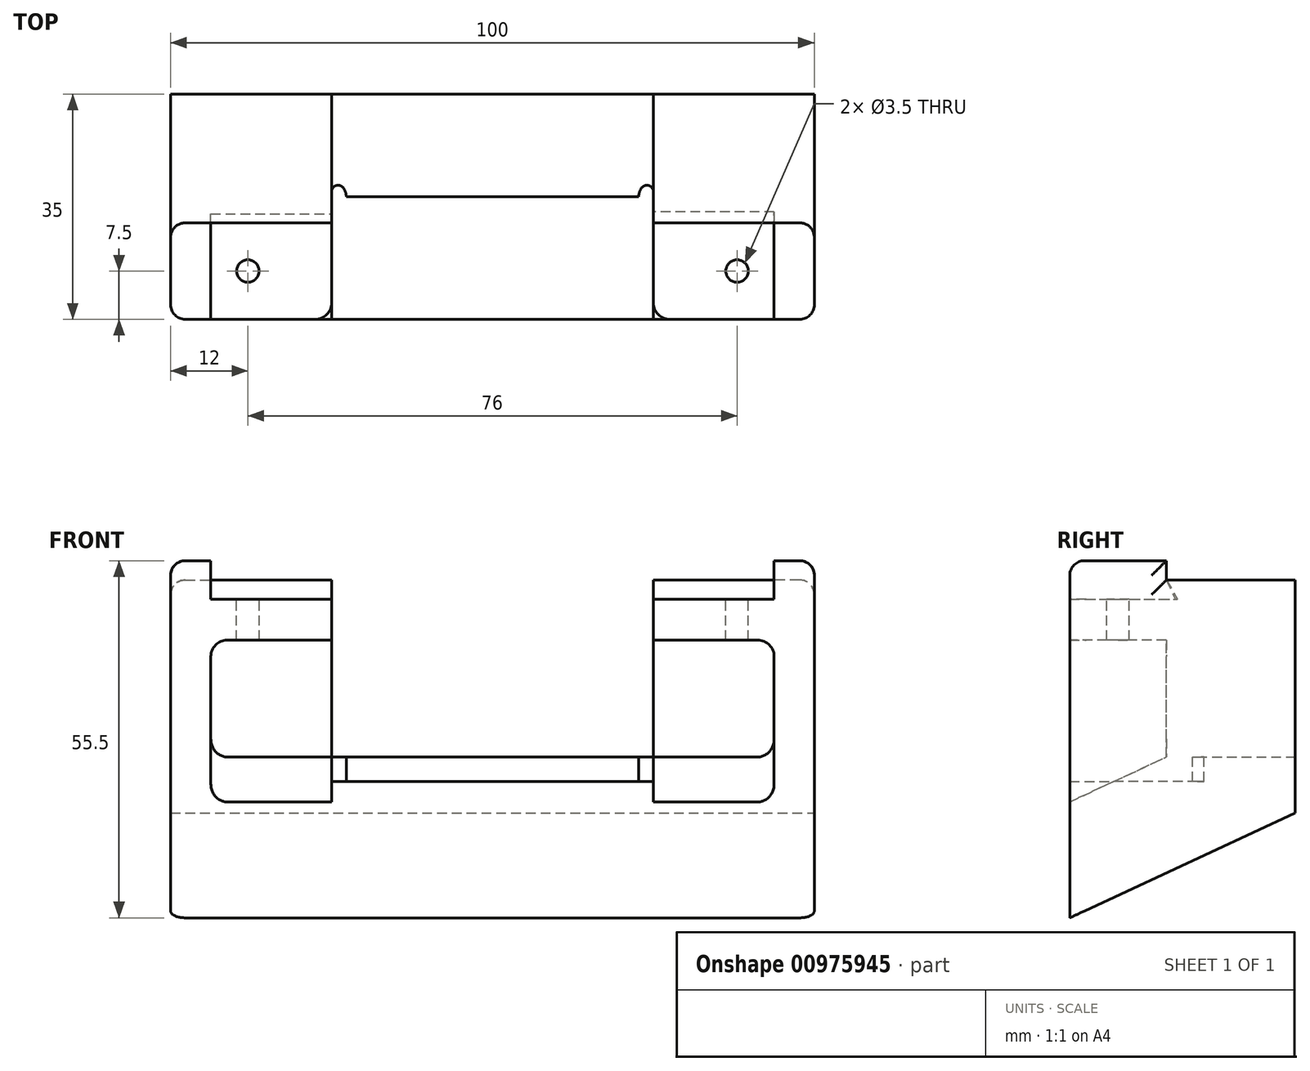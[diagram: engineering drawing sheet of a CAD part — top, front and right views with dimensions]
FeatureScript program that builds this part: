
annotation { "Feature Type Name" : "Feature", "Feature Type Description" : "" }
export const myFeature = defineFeature(function(context is Context, id is Id, definition is map)
    precondition{}
    {
        {
            var Q0;
            Q0=qCreatedBy(makeId("Front.planeOp"),FACE);
            var sketch = newSketch(context, id + "F0", { "sketchPlane" : qUnion([Q0])});
            skLineSegment(sketch, "E0", {"start": v(0, 0) * mm, "end": v(0, 100) * mm, "construction": true});
            skLineSegment(sketch, "E1", {"start": v(0, 25) * mm, "end": v(-25, 25) * mm});
            skLineSegment(sketch, "E2", {"start": v(-25, 25) * mm, "end": v(-25, 49.5) * mm});
            skLineSegment(sketch, "E3", {"start": v(-25, 49.5) * mm, "end": v(-43.75, 49.5) * mm});
            skLineSegment(sketch, "E4", {"start": v(-43.75, 49.5) * mm, "end": v(-43.75, 55.5) * mm});
            skLineSegment(sketch, "E5", {"start": v(-43.75, 55.5) * mm, "end": v(-50, 55.5) * mm});
            skLineSegment(sketch, "E6", {"start": v(-50, 55.5) * mm, "end": v(-50, 0) * mm});
            skLineSegment(sketch, "E7", {"start": v(-50, 0) * mm, "end": v(0, 0) * mm});
            skLineSegment(sketch, "E8.MirrorCS", {"start": v(25, 25) * mm, "end": v(25, 49.5) * mm});
            skLineSegment(sketch, "E9.MirrorCS", {"start": v(50, 55.5) * mm, "end": v(50, 0) * mm});
            skLineSegment(sketch, "E10.MirrorCS", {"start": v(0, 25) * mm, "end": v(25, 25) * mm});
            skLineSegment(sketch, "E11.MirrorCS", {"start": v(43.75, 55.5) * mm, "end": v(50, 55.5) * mm});
            skLineSegment(sketch, "E12.MirrorCS", {"start": v(25, 49.5) * mm, "end": v(43.75, 49.5) * mm});
            skLineSegment(sketch, "E13.MirrorCS", {"start": v(43.75, 49.5) * mm, "end": v(43.75, 55.5) * mm});
            skLineSegment(sketch, "E14.MirrorCS", {"start": v(50, 0) * mm, "end": v(0, 0) * mm});
            skSolve(sketch);
        }
        {
            var Q0;
            Q0 = qSketchRegion(id + "F0", true);
            extrude(context, id + "F1", {"entities" : qUnion([Q0]), "depth" : 15 * mm, "offsetDistance" : 25.4 * mm});
        }
        {
            var Q0;
            Q0=makeQuery(id+"F1.opExtrude","CAP_FACE",FACE,{"disambiguationData":[OSD([sQuery(id+"F0.wireOp",EDGE,"E1"),sQuery(id+"F0.wireOp",EDGE,"E2"),sQuery(id+"F0.wireOp",EDGE,"E3"),sQuery(id+"F0.wireOp",EDGE,"E4"),sQuery(id+"F0.wireOp",EDGE,"E5"),sQuery(id+"F0.wireOp",EDGE,"E6"),sQuery(id+"F0.wireOp",EDGE,"E7"),sQuery(id+"F0.wireOp",EDGE,"E8.MirrorCS"),sQuery(id+"F0.wireOp",EDGE,"E9.MirrorCS"),sQuery(id+"F0.wireOp",EDGE,"E10.MirrorCS"),sQuery(id+"F0.wireOp",EDGE,"E11.MirrorCS"),sQuery(id+"F0.wireOp",EDGE,"E12.MirrorCS"),sQuery(id+"F0.wireOp",EDGE,"E13.MirrorCS"),sQuery(id+"F0.wireOp",EDGE,"E14.MirrorCS")])],"isStart":true});
            var sketch = newSketch(context, id + "F2", { "sketchPlane" : qUnion([Q0])});
            skLineSegment(sketch, "E15.0", {"start": v(-50, 52.5) * mm, "end": v(-50, 0) * mm});
            skLineSegment(sketch, "E15.1", {"start": v(0, 0) * mm, "end": v(-50, 0) * mm});
            skLineSegment(sketch, "E16", {"start": v(-50, 52.5) * mm, "end": v(-25, 52.5) * mm});
            skLineSegment(sketch, "E17", {"start": v(-25, 52.5) * mm, "end": v(-25, 25) * mm});
            skLineSegment(sketch, "E18", {"start": v(-25, 25) * mm, "end": v(0, 25) * mm});
            skLineSegment(sketch, "E19", {"start": v(0, 0) * mm, "end": v(0, 25) * mm, "construction": true});
            skLineSegment(sketch, "E20.MirrorCS", {"start": v(25, 25) * mm, "end": v(0, 25) * mm});
            skLineSegment(sketch, "E21.MirrorCS", {"start": v(25, 52.5) * mm, "end": v(25, 25) * mm});
            skLineSegment(sketch, "E22.MirrorCS", {"start": v(50, 52.5) * mm, "end": v(25, 52.5) * mm});
            skLineSegment(sketch, "E23.MirrorCS", {"start": v(50, 52.5) * mm, "end": v(50, 0) * mm});
            skLineSegment(sketch, "E24.MirrorCS", {"start": v(0, 0) * mm, "end": v(50, 0) * mm});
            skPoint(sketch, "E25.orphan", {"position": v(-50, 55.5) * mm});
            skPoint(sketch, "E26.orphan", {"position": v(50, 55.5) * mm});
            skSolve(sketch);
        }
        {
            var Q0;
            Q0 = qSketchRegion(id + "F2", true);
            extrude(context, id + "F3", {"entities" : qUnion([Q0]), "operationType" : NewBodyOperationType.ADD, "depth" : 20 * mm, "offsetDistance" : 25.4 * mm});
        }
        {
            var Q0;
            Q0=makeQuery(id+"F3.boolean.opBoolean","MERGE",FACE,{"derivedFrom":[makeQuery(id+"F1.opExtrude","SWEPT_FACE",FACE,{"disambiguationData":[OSD([sQuery(id+"F0.wireOp",EDGE,"E9.MirrorCS")])]}),makeQuery(id+"F3.opExtrude","SWEPT_FACE",FACE,{"disambiguationData":[OSD([sQuery(id+"F2.wireOp",EDGE,"E15.0")])]})]});
            var sketch = newSketch(context, id + "F4", { "sketchPlane" : qUnion([Q0])});
            skLineSegment(sketch, "E27", {"start": v(20, 0) * mm, "end": v(-15, 0) * mm});
            skLineSegment(sketch, "E28", {"start": v(-15, 0) * mm, "end": v(20, 16.32) * mm});
            skLineSegment(sketch, "E29", {"start": v(20, 16.32) * mm, "end": v(20, 0) * mm});
            skSolve(sketch);
        }
        {
            var Q0;
            Q0 = qSketchRegion(id + "F4", true);
            extrude(context, id + "F5", {"entities" : qUnion([Q0]), "operationType" : NewBodyOperationType.REMOVE, "endBound" : BoundingType.UP_TO_NEXT, "oppositeDirection" : true, "depth" : 25.4 * mm, "offsetDistance" : 25.4 * mm});
        }
        {
            var Q0;
            Q0=makeQuery(id+"F3.boolean.opBoolean","MERGE",FACE,{"derivedFrom":[makeQuery(id+"F1.opExtrude","SWEPT_FACE",FACE,{"disambiguationData":[OSD([sQuery(id+"F0.wireOp",EDGE,"E6")])]}),makeQuery(id+"F3.opExtrude","SWEPT_FACE",FACE,{"disambiguationData":[OSD([sQuery(id+"F2.wireOp",EDGE,"E23.MirrorCS")])]})]});
            cPlane(context, id + "F6", {"entities" : qUnion([Q0]), "cplaneType" : CPlaneType.OFFSET, "offset" : 56 * mm, "oppositeDirection" : true, "width" : 152.4 * mm, "height" : 152.4 * mm});
        }
        {
            var Q0;
            Q0=makeQuery(id+"F1.opExtrude","CAP_FACE",FACE,{"disambiguationData":[OSD([sQuery(id+"F0.wireOp",EDGE,"E1"),sQuery(id+"F0.wireOp",EDGE,"E2"),sQuery(id+"F0.wireOp",EDGE,"E3"),sQuery(id+"F0.wireOp",EDGE,"E4"),sQuery(id+"F0.wireOp",EDGE,"E5"),sQuery(id+"F0.wireOp",EDGE,"E6"),sQuery(id+"F0.wireOp",EDGE,"E7"),sQuery(id+"F0.wireOp",EDGE,"E8.MirrorCS"),sQuery(id+"F0.wireOp",EDGE,"E9.MirrorCS"),sQuery(id+"F0.wireOp",EDGE,"E10.MirrorCS"),sQuery(id+"F0.wireOp",EDGE,"E11.MirrorCS"),sQuery(id+"F0.wireOp",EDGE,"E12.MirrorCS"),sQuery(id+"F0.wireOp",EDGE,"E13.MirrorCS"),sQuery(id+"F0.wireOp",EDGE,"E14.MirrorCS")])],"isStart":false});
            var sketch = newSketch(context, id + "F7", { "sketchPlane" : qUnion([Q0])});
            skLineSegment(sketch, "E30", {"start": v(0, 25) * mm, "end": v(0, 49.5) * mm, "construction": true});
            skLineSegment(sketch, "E31.bottom", {"start": v(-25, 25) * mm, "end": v(-43.75, 25) * mm});
            skLineSegment(sketch, "E31.top", {"start": v(-25, 43.15) * mm, "end": v(-43.75, 43.15) * mm});
            skLineSegment(sketch, "E31.left", {"start": v(-25, 25) * mm, "end": v(-25, 43.15) * mm});
            skLineSegment(sketch, "E31.right", {"start": v(-43.75, 25) * mm, "end": v(-43.75, 43.15) * mm});
            skLineSegment(sketch, "E32.MirrorCS", {"start": v(43.75, 25) * mm, "end": v(43.75, 43.15) * mm});
            skLineSegment(sketch, "E33.MirrorCS", {"start": v(25, 25) * mm, "end": v(43.75, 25) * mm});
            skLineSegment(sketch, "E34.MirrorCS", {"start": v(25, 25) * mm, "end": v(25, 43.15) * mm});
            skLineSegment(sketch, "E35.MirrorCS", {"start": v(25, 43.15) * mm, "end": v(43.75, 43.15) * mm});
            skSolve(sketch);
        }
        {
            var Q0;
            Q0 = qSketchRegion(id + "F7", true);
            var Q1;
            {var subQ1=sQuery(id+"F0.wireOp",EDGE,"E2");var subQ3=sQuery(id+"F2.wireOp",EDGE,"E21.MirrorCS");var subQ4=sQuery(id+"F2.wireOp",EDGE,"E22.MirrorCS");Q1=makeQuery(id+"F3.boolean.opBoolean","SPLIT",FACE,{"disambiguationData":[TD([makeQuery(id+"F1.opExtrude","SWEPT_FACE",FACE,{"disambiguationData":[OSD([subQ1])]})])],"derivedFrom":makeQuery(id+"F3.opExtrude","CAP_FACE",FACE,{"disambiguationData":[OSD([sQuery(id+"F2.wireOp",EDGE,"E15.0"),sQuery(id+"F2.wireOp",EDGE,"E15.1"),sQuery(id+"F2.wireOp",EDGE,"E16"),sQuery(id+"F2.wireOp",EDGE,"E17"),sQuery(id+"F2.wireOp",EDGE,"E18"),sQuery(id+"F2.wireOp",EDGE,"E20.MirrorCS"),subQ3,subQ4,sQuery(id+"F2.wireOp",EDGE,"E23.MirrorCS"),sQuery(id+"F2.wireOp",EDGE,"E24.MirrorCS")])],"isStart":true})});}
            extrude(context, id + "F8", {"entities" : qUnion([Q0]), "operationType" : NewBodyOperationType.REMOVE, "endBound" : BoundingType.UP_TO_SURFACE, "oppositeDirection" : true, "depth" : 25.4 * mm, "endBoundEntityFace" : qUnion([Q1]), "offsetDistance" : 25.4 * mm});
        }
        {
            var Q0;
            Q0=makeQuery(id+"F8.boolean.opBoolean","COPY",FACE,{"derivedFrom":makeQuery(id+"F8.opExtrude","SWEPT_FACE",FACE,{"disambiguationData":[OSD([sQuery(id+"F7.wireOp",EDGE,"E31.right")])]})});
            var sketch = newSketch(context, id + "F9", { "sketchPlane" : qUnion([Q0])});
            skLineSegment(sketch, "E36", {"start": v(0, 25) * mm, "end": v(-15, 25) * mm});
            skLineSegment(sketch, "E37", {"start": v(-15, 25) * mm, "end": v(-15, 18) * mm});
            skLineSegment(sketch, "E38", {"start": v(-15, 18) * mm, "end": v(0, 25) * mm});
            skSolve(sketch);
        }
        {
            var Q0;
            Q0 = qSketchRegion(id + "F9", true);
            var Q1;
            Q1=makeQuery(id+"F3.boolean.opBoolean","MERGE",FACE,{"derivedFrom":[makeQuery(id+"F1.opExtrude","SWEPT_FACE",FACE,{"disambiguationData":[OSD([sQuery(id+"F0.wireOp",EDGE,"E2")])]}),makeQuery(id+"F3.opExtrude","SWEPT_FACE",FACE,{"disambiguationData":[OSD([sQuery(id+"F2.wireOp",EDGE,"E21.MirrorCS")])]})]});
            extrude(context, id + "F10", {"entities" : qUnion([Q0]), "operationType" : NewBodyOperationType.REMOVE, "endBound" : BoundingType.UP_TO_SURFACE, "depth" : 25.4 * mm, "endBoundEntityFace" : qUnion([Q1]), "offsetDistance" : 25.4 * mm});
        }
        {
            var Q0;
            Q0=makeQuery(id+"F8.boolean.opBoolean","COPY",FACE,{"derivedFrom":makeQuery(id+"F8.opExtrude","SWEPT_FACE",FACE,{"disambiguationData":[OSD([sQuery(id+"F7.wireOp",EDGE,"E32.MirrorCS")])]})});
            var sketch = newSketch(context, id + "F11", { "sketchPlane" : qUnion([Q0])});
            skLineSegment(sketch, "E39", {"start": v(0, 25) * mm, "end": v(15, 25) * mm});
            skLineSegment(sketch, "E40", {"start": v(15, 25) * mm, "end": v(15, 18) * mm});
            skLineSegment(sketch, "E41", {"start": v(15, 18) * mm, "end": v(0, 25) * mm});
            skSolve(sketch);
        }
        {
            var Q0;
            Q0 = qSketchRegion(id + "F11", true);
            var Q1;
            Q1=makeQuery(id+"F3.boolean.opBoolean","MERGE",FACE,{"derivedFrom":[makeQuery(id+"F1.opExtrude","SWEPT_FACE",FACE,{"disambiguationData":[OSD([sQuery(id+"F0.wireOp",EDGE,"E8.MirrorCS")])]}),makeQuery(id+"F3.opExtrude","SWEPT_FACE",FACE,{"disambiguationData":[OSD([sQuery(id+"F2.wireOp",EDGE,"E17")])]})]});
            extrude(context, id + "F12", {"entities" : qUnion([Q0]), "operationType" : NewBodyOperationType.REMOVE, "endBound" : BoundingType.UP_TO_SURFACE, "depth" : 25.4 * mm, "endBoundEntityFace" : qUnion([Q1]), "offsetDistance" : 25.4 * mm});
        }
        {
            var Q0;
            Q0=makeQuery(id+"F10.boolean.opBoolean","COPY",EDGE,{"derivedFrom":makeQuery(id+"F10.opExtrude","CAP_EDGE",EDGE,{"disambiguationData":[OSD([sQuery(id+"F9.wireOp",EDGE,"E38")])],"isStart":true})});
            var Q1;
            Q1=makeQuery(id+"F10.boolean.opBoolean","COPY",EDGE,{"derivedFrom":makeQuery(id+"F10.opExtrude","CAP_EDGE",EDGE,{"disambiguationData":[OSD([sQuery(id+"F9.wireOp",EDGE,"E37")])],"isStart":false})});
            var Q2;
            Q2=makeQuery(id+"F10.boolean.opBoolean","COPY",EDGE,{"derivedFrom":makeQuery(id+"F10.opExtrude","SWEPT_EDGE",EDGE,{"disambiguationData":[OSD([sQuery(id+"F9.wireOp",EDGE,"E37"),sQuery(id+"F9.wireOp",EDGE,"E38")])]})});
            var Q3;
            Q3=makeQuery(id+"F8.boolean.opBoolean","COPY",EDGE,{"derivedFrom":makeQuery(id+"F8.opExtrude","SWEPT_EDGE",EDGE,{"disambiguationData":[OSD([sQuery(id+"F7.wireOp",EDGE,"E31.top"),sQuery(id+"F7.wireOp",EDGE,"E31.right")])]})});
            var Q4;
            Q4=makeQuery(id+"F12.boolean.opBoolean","COPY",EDGE,{"derivedFrom":makeQuery(id+"F12.opExtrude","CAP_EDGE",EDGE,{"disambiguationData":[OSD([sQuery(id+"F11.wireOp",EDGE,"E40")])],"isStart":false})});
            var Q5;
            Q5=makeQuery(id+"F12.boolean.opBoolean","COPY",EDGE,{"derivedFrom":makeQuery(id+"F12.opExtrude","SWEPT_EDGE",EDGE,{"disambiguationData":[OSD([sQuery(id+"F11.wireOp",EDGE,"E40"),sQuery(id+"F11.wireOp",EDGE,"E41")])]})});
            var Q6;
            Q6=makeQuery(id+"F12.boolean.opBoolean","MERGE",EDGE,{"derivedFrom":[makeQuery(id+"F8.boolean.opBoolean","COPY",EDGE,{"derivedFrom":makeQuery(id+"F8.opExtrude","CAP_EDGE",EDGE,{"disambiguationData":[OSD([sQuery(id+"F7.wireOp",EDGE,"E32.MirrorCS")])],"isStart":true})})],"fromTools":[makeQuery(id+"F12.opExtrude","CAP_EDGE",EDGE,{"disambiguationData":[OSD([sQuery(id+"F11.wireOp",EDGE,"E40")])],"isStart":true})]});
            var Q7;
            Q7=makeQuery(id+"F8.boolean.opBoolean","COPY",EDGE,{"derivedFrom":makeQuery(id+"F8.opExtrude","CAP_EDGE",EDGE,{"disambiguationData":[OSD([sQuery(id+"F7.wireOp",EDGE,"E35.MirrorCS")])],"isStart":true})});
            var Q8;
            Q8=makeQuery(id+"F8.boolean.opBoolean","COPY",EDGE,{"derivedFrom":makeQuery(id+"F8.opExtrude","SWEPT_EDGE",EDGE,{"disambiguationData":[OSD([sQuery(id+"F7.wireOp",EDGE,"E32.MirrorCS"),sQuery(id+"F7.wireOp",EDGE,"E35.MirrorCS")])]})});
            var Q9;
            Q9=makeQuery(id+"F12.boolean.opBoolean","COPY",EDGE,{"derivedFrom":makeQuery(id+"F12.opExtrude","CAP_EDGE",EDGE,{"disambiguationData":[OSD([sQuery(id+"F11.wireOp",EDGE,"E41")])],"isStart":true})});
            var Q10;
            Q10=makeQuery(id+"F8.boolean.opBoolean","COPY",EDGE,{"derivedFrom":makeQuery(id+"F8.opExtrude","SWEPT_EDGE",EDGE,{"disambiguationData":[OSD([sQuery(id+"F0.wireOp",EDGE,"E2"),sQuery(id+"F7.wireOp",EDGE,"E31.top"),sQuery(id+"F7.wireOp",EDGE,"E31.left")])]})});
            var Q11;
            Q11=makeQuery(id+"F8.boolean.opBoolean","COPY",EDGE,{"derivedFrom":makeQuery(id+"F8.opExtrude","SWEPT_EDGE",EDGE,{"disambiguationData":[OSD([sQuery(id+"F0.wireOp",EDGE,"E8.MirrorCS"),sQuery(id+"F7.wireOp",EDGE,"E34.MirrorCS"),sQuery(id+"F7.wireOp",EDGE,"E35.MirrorCS")])]})});
            var Q12;
            Q12=makeQuery(id+"F1.opExtrude","CAP_EDGE",EDGE,{"disambiguationData":[OSD([sQuery(id+"F0.wireOp",EDGE,"E2")])],"isStart":false});
            var Q13;
            Q13=makeQuery(id+"F1.opExtrude","CAP_EDGE",EDGE,{"disambiguationData":[OSD([sQuery(id+"F0.wireOp",EDGE,"E8.MirrorCS")])],"isStart":false});
            var Q14;
            Q14=makeQuery(id+"F8.boolean.opBoolean","COPY",EDGE,{"derivedFrom":makeQuery(id+"F8.opExtrude","CAP_EDGE",EDGE,{"disambiguationData":[OSD([sQuery(id+"F7.wireOp",EDGE,"E31.left")])],"isStart":false})});
            var Q15;
            Q15=makeQuery(id+"F8.boolean.opBoolean","COPY",EDGE,{"derivedFrom":makeQuery(id+"F8.opExtrude","CAP_EDGE",EDGE,{"disambiguationData":[OSD([sQuery(id+"F7.wireOp",EDGE,"E34.MirrorCS")])],"isStart":false})});
            fillet(context, id + "F13", {"entities" : qUnion([Q0, Q1, Q2, Q3, Q4, Q5, Q6, Q7, Q8, Q9, Q10, Q11, Q12, Q13, Q14, Q15]), "radius" : 2.54 * mm, "tangentPropagation" : true, "allowEdgeOverflow" : false});
        }
        {
            var Q0;
            Q0=makeQuery(id+"F1.opExtrude","SWEPT_FACE",FACE,{"disambiguationData":[OSD([sQuery(id+"F0.wireOp",EDGE,"E3")])]});
            var sketch = newSketch(context, id + "F14", { "sketchPlane" : qUnion([Q0])});
            skLineSegment(sketch, "E42", {"start": v(-43.75, -7.5) * mm, "end": v(43.75, -7.5) * mm, "construction": true});
            skLineSegment(sketch, "E43", {"start": v(0, -7.5) * mm, "end": v(0, 20) * mm, "construction": true});
            skPoint(sketch, "E44", {"position": v(-38, -7.5) * mm});
            skPoint(sketch, "E45", {"position": v(38, -7.5) * mm});
            skSolve(sketch);
        }
        {
            var Q0;
            Q0=sQuery(id+"F14.wireOp",VERTEX,"E44");
            var Q1;
            Q1=sQuery(id+"F14.wireOp",VERTEX,"E45");
            var Q2;
            Q2=makeQuery(id+"F1.opExtrude","SWEPT_BODY",BODY,{"disambiguationData":[OSD([sQuery(id+"F0.wireOp",EDGE,"E1"),sQuery(id+"F0.wireOp",EDGE,"E2"),sQuery(id+"F0.wireOp",EDGE,"E3"),sQuery(id+"F0.wireOp",EDGE,"E4"),sQuery(id+"F0.wireOp",EDGE,"E5"),sQuery(id+"F0.wireOp",EDGE,"E6"),sQuery(id+"F0.wireOp",EDGE,"E7"),sQuery(id+"F0.wireOp",EDGE,"E8.MirrorCS"),sQuery(id+"F0.wireOp",EDGE,"E9.MirrorCS"),sQuery(id+"F0.wireOp",EDGE,"E10.MirrorCS"),sQuery(id+"F0.wireOp",EDGE,"E11.MirrorCS"),sQuery(id+"F0.wireOp",EDGE,"E12.MirrorCS"),sQuery(id+"F0.wireOp",EDGE,"E13.MirrorCS"),sQuery(id+"F0.wireOp",EDGE,"E14.MirrorCS")])]});
            hole(context, id + "F15", {"style" : HoleStyle.SIMPLE, "endStyle" : HoleEndStyle.BLIND, "holeDiameter" : 3.5 * mm, "majorDiameter" : 6.35 * mm, "holeDepth" : 12.7 * mm, "isTappedThrough" : true, "tappedDepth" : 12.7 * mm, "tapClearance" : 3, "locations" : qUnion([Q0, Q1]), "scope" : qUnion([Q2])});
        }
        {
            var Q0;
            Q0=makeQuery(id+"F8.boolean.opBoolean","MERGE",FACE,{"derivedFrom":[makeQuery(id+"F3.boolean.opBoolean","MERGE",FACE,{"derivedFrom":[makeQuery(id+"F1.opExtrude","SWEPT_FACE",FACE,{"disambiguationData":[OSD([sQuery(id+"F0.wireOp",EDGE,"E1"),sQuery(id+"F0.wireOp",EDGE,"E10.MirrorCS")])]}),makeQuery(id+"F3.opExtrude","SWEPT_FACE",FACE,{"disambiguationData":[OSD([sQuery(id+"F2.wireOp",EDGE,"E18"),sQuery(id+"F2.wireOp",EDGE,"E20.MirrorCS")])]})]})],"fromTools":[makeQuery(id+"F8.opExtrude","SWEPT_FACE",FACE,{"disambiguationData":[OSD([sQuery(id+"F7.wireOp",EDGE,"E31.bottom")])]}),makeQuery(id+"F8.opExtrude","SWEPT_FACE",FACE,{"disambiguationData":[OSD([sQuery(id+"F7.wireOp",EDGE,"E33.MirrorCS")])]})]});
            var sketch = newSketch(context, id + "F16", { "sketchPlane" : qUnion([Q0])});
            skLineSegment(sketch, "E46.bottom", {"start": v(-25, 4.05) * mm, "end": v(25, 4.05) * mm});
            skLineSegment(sketch, "E46.top", {"start": v(-25, -15) * mm, "end": v(25, -15) * mm});
            skLineSegment(sketch, "E46.left", {"start": v(-25, 4.05) * mm, "end": v(-25, -15) * mm});
            skLineSegment(sketch, "E46.right", {"start": v(25, 4.05) * mm, "end": v(25, -15) * mm});
            skSolve(sketch);
        }
        {
            var Q0;
            Q0 = qSketchRegion(id + "F16", true);
            extrude(context, id + "F17", {"entities" : qUnion([Q0]), "operationType" : NewBodyOperationType.REMOVE, "oppositeDirection" : true, "depth" : 3.8 * mm, "offsetDistance" : 25.4 * mm});
        }
        {
            var Q0;
            Q0=makeQuery(id+"F8.boolean.opBoolean","MERGE",FACE,{"derivedFrom":[makeQuery(id+"F3.boolean.opBoolean","MERGE",FACE,{"derivedFrom":[makeQuery(id+"F1.opExtrude","SWEPT_FACE",FACE,{"disambiguationData":[OSD([sQuery(id+"F0.wireOp",EDGE,"E1"),sQuery(id+"F0.wireOp",EDGE,"E10.MirrorCS")])]}),makeQuery(id+"F3.opExtrude","SWEPT_FACE",FACE,{"disambiguationData":[OSD([sQuery(id+"F2.wireOp",EDGE,"E18"),sQuery(id+"F2.wireOp",EDGE,"E20.MirrorCS")])]})]})],"fromTools":[makeQuery(id+"F8.opExtrude","SWEPT_FACE",FACE,{"disambiguationData":[OSD([sQuery(id+"F7.wireOp",EDGE,"E31.bottom")])]}),makeQuery(id+"F8.opExtrude","SWEPT_FACE",FACE,{"disambiguationData":[OSD([sQuery(id+"F7.wireOp",EDGE,"E33.MirrorCS")])]})]});
            var sketch = newSketch(context, id + "F18", { "sketchPlane" : qUnion([Q0])});
            skLineSegment(sketch, "E47", {"start": v(0, 4.05) * mm, "end": v(0, 20) * mm, "construction": true});
            skLineSegment(sketch, "E48", {"start": v(-22.71, 4.05) * mm, "end": v(-25, 4.05) * mm});
            skLineSegment(sketch, "E49", {"start": v(-25, 4.05) * mm, "end": v(-25, 6.34) * mm});
            skArc(sketch, "E50", {"start": v(-22.71, 4.05) * mm, "mid": v(-23.38, 5.67) * mm, "end": v(-25, 6.34) * mm});
            skLineSegment(sketch, "E51.MirrorCS", {"start": v(25, 4.05) * mm, "end": v(25, 6.34) * mm});
            skLineSegment(sketch, "E52.MirrorCS", {"start": v(22.71, 4.05) * mm, "end": v(25, 4.05) * mm});
            skArc(sketch, "E53.MirrorCS", {"start": v(22.71, 4.05) * mm, "mid": v(23.38, 5.67) * mm, "end": v(25, 6.34) * mm});
            skSolve(sketch);
        }
        {
            var Q0;
            Q0 = qSketchRegion(id + "F18", true);
            var Q1;
            Q1=makeQuery(id+"F17.boolean.opBoolean","COPY",FACE,{"derivedFrom":makeQuery(id+"F17.opExtrude","CAP_FACE",FACE,{"disambiguationData":[OSD([sQuery(id+"F16.wireOp",EDGE,"E46.bottom"),sQuery(id+"F16.wireOp",EDGE,"E46.top"),sQuery(id+"F16.wireOp",EDGE,"E46.left"),sQuery(id+"F16.wireOp",EDGE,"E46.right")])],"isStart":false})});
            extrude(context, id + "F19", {"entities" : qUnion([Q0]), "operationType" : NewBodyOperationType.REMOVE, "endBound" : BoundingType.UP_TO_SURFACE, "oppositeDirection" : true, "depth" : 25.4 * mm, "endBoundEntityFace" : qUnion([Q1]), "offsetDistance" : 25.4 * mm});
        }
        {
            var Q0;
            Q0=makeQuery(id+"F19.boolean.opBoolean","COPY",EDGE,{"derivedFrom":makeQuery(id+"F19.opExtrude","SWEPT_EDGE",EDGE,{"disambiguationData":[OSD([sQuery(id+"F0.wireOp",EDGE,"E1"),sQuery(id+"F0.wireOp",EDGE,"E2"),sQuery(id+"F2.wireOp",EDGE,"E20.MirrorCS"),sQuery(id+"F2.wireOp",EDGE,"E21.MirrorCS"),sQuery(id+"F18.wireOp",EDGE,"E49"),sQuery(id+"F18.wireOp",EDGE,"E50")])]})});
            var Q1;
            Q1=makeQuery(id+"F19.boolean.opBoolean","COPY",EDGE,{"derivedFrom":makeQuery(id+"F19.opExtrude","SWEPT_EDGE",EDGE,{"disambiguationData":[OSD([sQuery(id+"F0.wireOp",EDGE,"E8.MirrorCS"),sQuery(id+"F0.wireOp",EDGE,"E10.MirrorCS"),sQuery(id+"F2.wireOp",EDGE,"E17"),sQuery(id+"F2.wireOp",EDGE,"E18"),sQuery(id+"F18.wireOp",EDGE,"E51.MirrorCS"),sQuery(id+"F18.wireOp",EDGE,"E53.MirrorCS")])]})});
            var Q2;
            Q2=makeQuery(id+"F19.boolean.opBoolean","COPY",EDGE,{"derivedFrom":makeQuery(id+"F19.opExtrude","SWEPT_EDGE",EDGE,{"disambiguationData":[OSD([sQuery(id+"F16.wireOp",EDGE,"E46.bottom"),sQuery(id+"F18.wireOp",EDGE,"E48"),sQuery(id+"F18.wireOp",EDGE,"E50")])]})});
            var Q3;
            Q3=makeQuery(id+"F19.boolean.opBoolean","COPY",EDGE,{"derivedFrom":makeQuery(id+"F19.opExtrude","SWEPT_EDGE",EDGE,{"disambiguationData":[OSD([sQuery(id+"F16.wireOp",EDGE,"E46.bottom"),sQuery(id+"F18.wireOp",EDGE,"E52.MirrorCS"),sQuery(id+"F18.wireOp",EDGE,"E53.MirrorCS")])]})});
            fillet(context, id + "F20", {"entities" : qUnion([Q0, Q1, Q2, Q3]), "radius" : 1.02 * mm, "tangentPropagation" : true, "allowEdgeOverflow" : false});
        }
        {
            var Q0;
            Q0=makeQuery(id+"F19.boolean.opBoolean","MERGE",FACE,{"derivedFrom":[makeQuery(id+"F17.boolean.opBoolean","MERGE",FACE,{"derivedFrom":[makeQuery(id+"F3.boolean.opBoolean","MERGE",FACE,{"derivedFrom":[makeQuery(id+"F1.opExtrude","SWEPT_FACE",FACE,{"disambiguationData":[OSD([sQuery(id+"F0.wireOp",EDGE,"E2")])]}),makeQuery(id+"F3.opExtrude","SWEPT_FACE",FACE,{"disambiguationData":[OSD([sQuery(id+"F2.wireOp",EDGE,"E21.MirrorCS")])]})]})],"fromTools":[makeQuery(id+"F17.opExtrude","SWEPT_FACE",FACE,{"disambiguationData":[OSD([sQuery(id+"F16.wireOp",EDGE,"E46.left")])]})]})],"fromTools":[makeQuery(id+"F19.opExtrude","SWEPT_FACE",FACE,{"disambiguationData":[OSD([sQuery(id+"F18.wireOp",EDGE,"E49")])]})]});
            var sketch = newSketch(context, id + "F21", { "sketchPlane" : qUnion([Q0])});
            skLineSegment(sketch, "E54", {"start": v(0, 52.5) * mm, "end": v(1.4, 49.5) * mm});
            skLineSegment(sketch, "E55", {"start": v(1.4, 49.5) * mm, "end": v(0, 49.5) * mm});
            skLineSegment(sketch, "E56", {"start": v(0, 49.5) * mm, "end": v(0, 52.5) * mm});
            skSolve(sketch);
        }
        {
            var Q0;
            Q0 = qSketchRegion(id + "F21", true);
            var Q1;
            Q1=makeQuery(id+"F1.opExtrude","SWEPT_FACE",FACE,{"disambiguationData":[OSD([sQuery(id+"F0.wireOp",EDGE,"E4")])]});
            extrude(context, id + "F22", {"entities" : qUnion([Q0]), "operationType" : NewBodyOperationType.REMOVE, "endBound" : BoundingType.UP_TO_SURFACE, "oppositeDirection" : true, "depth" : 25.4 * mm, "endBoundEntityFace" : qUnion([Q1]), "offsetDistance" : 25.4 * mm});
        }
        {
            var Q0;
            Q0=makeQuery(id+"F19.boolean.opBoolean","MERGE",FACE,{"derivedFrom":[makeQuery(id+"F17.boolean.opBoolean","MERGE",FACE,{"derivedFrom":[makeQuery(id+"F3.boolean.opBoolean","MERGE",FACE,{"derivedFrom":[makeQuery(id+"F1.opExtrude","SWEPT_FACE",FACE,{"disambiguationData":[OSD([sQuery(id+"F0.wireOp",EDGE,"E8.MirrorCS")])]}),makeQuery(id+"F3.opExtrude","SWEPT_FACE",FACE,{"disambiguationData":[OSD([sQuery(id+"F2.wireOp",EDGE,"E17")])]})]})],"fromTools":[makeQuery(id+"F17.opExtrude","SWEPT_FACE",FACE,{"disambiguationData":[OSD([sQuery(id+"F16.wireOp",EDGE,"E46.right")])]})]})],"fromTools":[makeQuery(id+"F19.opExtrude","SWEPT_FACE",FACE,{"disambiguationData":[OSD([sQuery(id+"F18.wireOp",EDGE,"E51.MirrorCS")])]})]});
            var sketch = newSketch(context, id + "F23", { "sketchPlane" : qUnion([Q0])});
            skLineSegment(sketch, "E57", {"start": v(0, 52.5) * mm, "end": v(-1.7, 49.5) * mm});
            skLineSegment(sketch, "E58", {"start": v(-1.7, 49.5) * mm, "end": v(0, 49.5) * mm});
            skLineSegment(sketch, "E59", {"start": v(0, 49.5) * mm, "end": v(0, 52.5) * mm});
            skSolve(sketch);
        }
        {
            var Q0;
            Q0 = qSketchRegion(id + "F23", true);
            var Q1;
            Q1=makeQuery(id+"F1.opExtrude","SWEPT_FACE",FACE,{"disambiguationData":[OSD([sQuery(id+"F0.wireOp",EDGE,"E13.MirrorCS")])]});
            extrude(context, id + "F24", {"entities" : qUnion([Q0]), "operationType" : NewBodyOperationType.REMOVE, "endBound" : BoundingType.UP_TO_SURFACE, "oppositeDirection" : true, "depth" : 25.4 * mm, "endBoundEntityFace" : qUnion([Q1]), "offsetDistance" : 25.4 * mm});
        }
        {
            var Q0;
            Q0=makeQuery(id+"F1.opExtrude","CAP_EDGE",EDGE,{"disambiguationData":[OSD([sQuery(id+"F0.wireOp",EDGE,"E9.MirrorCS")])],"isStart":false});
            var Q1;
            Q1=makeQuery(id+"F1.opExtrude","CAP_EDGE",EDGE,{"disambiguationData":[OSD([sQuery(id+"F0.wireOp",EDGE,"E6")])],"isStart":false});
            var Q2;
            Q2=makeQuery(id+"F1.opExtrude","SWEPT_EDGE",EDGE,{"disambiguationData":[OSD([sQuery(id+"F0.wireOp",EDGE,"E9.MirrorCS"),sQuery(id+"F0.wireOp",EDGE,"E11.MirrorCS")])]});
            var Q3;
            Q3=makeQuery(id+"F3.opExtrude","SWEPT_EDGE",EDGE,{"disambiguationData":[OSD([sQuery(id+"F0.wireOp",EDGE,"E9.MirrorCS"),sQuery(id+"F2.wireOp",EDGE,"E15.0"),sQuery(id+"F2.wireOp",EDGE,"E16")])]});
            var Q4;
            Q4=makeQuery(id+"F1.opExtrude","CAP_EDGE",EDGE,{"disambiguationData":[OSD([sQuery(id+"F0.wireOp",EDGE,"E9.MirrorCS")])],"isStart":true});
            var Q5;
            Q5=makeQuery(id+"F3.opExtrude","SWEPT_EDGE",EDGE,{"disambiguationData":[OSD([sQuery(id+"F0.wireOp",EDGE,"E6"),sQuery(id+"F2.wireOp",EDGE,"E22.MirrorCS"),sQuery(id+"F2.wireOp",EDGE,"E23.MirrorCS")])]});
            var Q6;
            Q6=makeQuery(id+"F1.opExtrude","SWEPT_EDGE",EDGE,{"disambiguationData":[OSD([sQuery(id+"F0.wireOp",EDGE,"E5"),sQuery(id+"F0.wireOp",EDGE,"E6")])]});
            var Q7;
            Q7=makeQuery(id+"F1.opExtrude","CAP_EDGE",EDGE,{"disambiguationData":[OSD([sQuery(id+"F0.wireOp",EDGE,"E6")])],"isStart":true});
            var Q8;
            Q8=makeQuery(id+"F1.opExtrude","CAP_EDGE",EDGE,{"disambiguationData":[OSD([sQuery(id+"F0.wireOp",EDGE,"E5")])],"isStart":false});
            var Q9;
            Q9=makeQuery(id+"F1.opExtrude","CAP_EDGE",EDGE,{"disambiguationData":[OSD([sQuery(id+"F0.wireOp",EDGE,"E11.MirrorCS")])],"isStart":false});
            fillet(context, id + "F25", {"entities" : qUnion([Q0, Q1, Q2, Q3, Q4, Q5, Q6, Q7, Q8, Q9]), "radius" : 2.3 * mm, "tangentPropagation" : true, "allowEdgeOverflow" : false});
        }
    });
